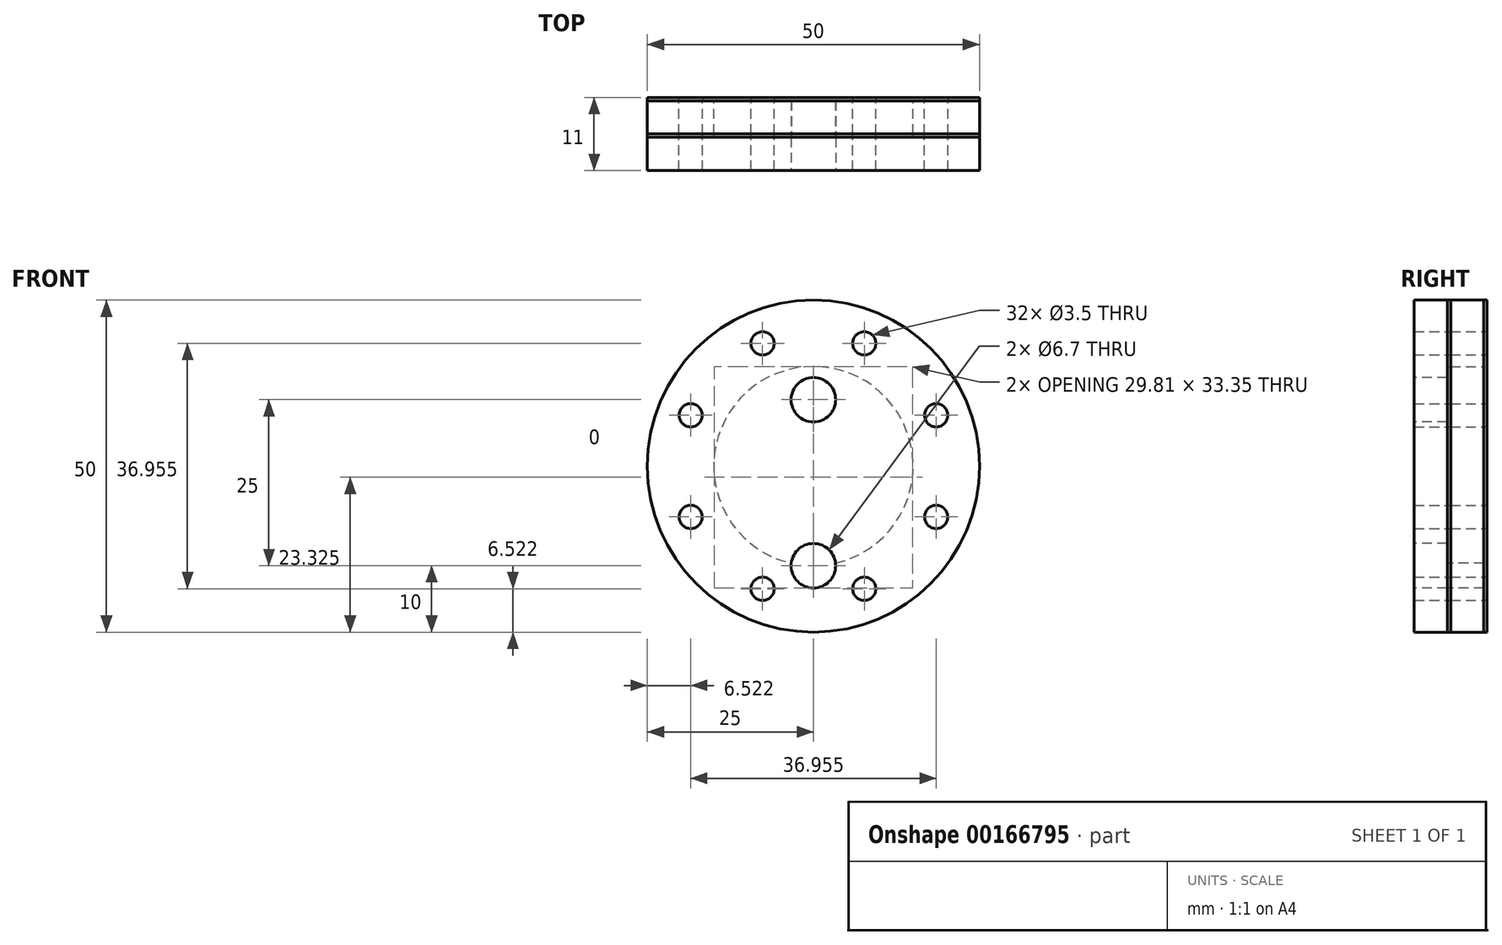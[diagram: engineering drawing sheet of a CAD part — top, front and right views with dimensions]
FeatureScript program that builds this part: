
annotation { "Feature Type Name" : "Feature", "Feature Type Description" : "" }
export const myFeature = defineFeature(function(context is Context, id is Id, definition is map)
    precondition{}
    {
        {
            var Q0;
            Q0=qCreatedBy(makeId("Front.planeOp"),FACE);
            var sketch = newSketch(context, id + "F0", { "sketchPlane" : qUnion([Q0])});
            skCircle(sketch, "E0", {"center": v(0, 0) * mm, "radius": 20 * mm, "construction": true});
            skCircle(sketch, "E1", {"center": v(7.65, -18.48) * mm, "radius": 1.75 * mm});
            skLineSegment(sketch, "E2", {"start": v(7.65, -18.48) * mm, "end": v(0, 0) * mm, "construction": true});
            skCircle(sketch, "E3.1.0", {"center": v(18.48, -7.65) * mm, "radius": 1.75 * mm});
            skCircle(sketch, "E3.2.0", {"center": v(18.48, 7.65) * mm, "radius": 1.75 * mm});
            skCircle(sketch, "E3.3.0", {"center": v(7.65, 18.48) * mm, "radius": 1.75 * mm});
            skCircle(sketch, "E3.4.0", {"center": v(-7.65, 18.48) * mm, "radius": 1.75 * mm});
            skCircle(sketch, "E3.5.0", {"center": v(-18.48, 7.65) * mm, "radius": 1.75 * mm});
            skCircle(sketch, "E3.6.0", {"center": v(-18.48, -7.65) * mm, "radius": 1.75 * mm});
            skCircle(sketch, "E3.7.0", {"center": v(-7.65, -18.48) * mm, "radius": 1.75 * mm});
            skSolve(sketch);
        }
        {
            var Q0;
            Q0=qCreatedBy(makeId("Front.planeOp"),FACE);
            var sketch = newSketch(context, id + "F1", { "sketchPlane" : qUnion([Q0])});
            skCircle(sketch, "E4", {"center": v(0, 0) * mm, "radius": 15 * mm});
            skCircle(sketch, "E5", {"center": v(0, 0) * mm, "radius": 25 * mm});
            skSolve(sketch);
        }
        {
            var Q0;
            Q0=makeQuery(id+"F1.imprint","IMPRINT",FACE,{"disambiguationData":[TD([[makeQuery(id+"F1.imprint","IMPRINT",EDGE,{"derivedFrom":sQuery(id+"F1.wireOp",EDGE,"E4")}),-1.0]])]});
            extrude(context, id + "F2", {"entities" : qUnion([Q0]), "depth" : 5 * mm});
        }
        {
            var Q0;
            Q0 = qSketchRegion(id + "F0", true);
            extrude(context, id + "F3", {"entities" : qUnion([Q0]), "operationType" : NewBodyOperationType.REMOVE, "endBound" : BoundingType.THROUGH_ALL, "depth" : 25 * mm});
        }
        {
            var Q0;
            Q0=makeQuery(id+"F2.opExtrude","CAP_FACE",FACE,{"disambiguationData":[OSD([sQuery(id+"F1.wireOp",EDGE,"E4"),sQuery(id+"F1.wireOp",EDGE,"E5")])],"isStart":false});
            extrude(context, id + "F4", {"entities" : qUnion([Q0]), "depth" : 0.5 * mm});
        }
        {
            var Q0;
            Q0=makeQuery(id+"F4.opExtrude","CAP_FACE",FACE,{"disambiguationData":[OSD([sQuery(id+"F1.wireOp",EDGE,"E4"),sQuery(id+"F1.wireOp",EDGE,"E5")])],"isStart":false});
            var sketch = newSketch(context, id + "F5", { "sketchPlane" : qUnion([Q0])});
            skCircle(sketch, "E6", {"center": v(0, 0) * mm, "radius": 25 * mm});
            skSolve(sketch);
        }
        {
            var Q0;
            Q0 = qSketchRegion(id + "F5", true);
            extrude(context, id + "F6", {"entities" : qUnion([Q0]), "depth" : 5 * mm});
        }
        {
            var Q0;
            Q0 = qSketchRegion(id + "F0", true);
            extrude(context, id + "F7", {"entities" : qUnion([Q0]), "operationType" : NewBodyOperationType.REMOVE, "endBound" : BoundingType.THROUGH_ALL, "depth" : 25 * mm});
        }
        {
            var Q0;
            Q0=makeQuery(id+"F6.opExtrude","CAP_FACE",FACE,{"disambiguationData":[OSD([sQuery(id+"F5.wireOp",EDGE,"E6")])],"isStart":false});
            var sketch = newSketch(context, id + "F8", { "sketchPlane" : qUnion([Q0])});
            skCircle(sketch, "E7", {"center": v(0, 10) * mm, "radius": 3.35 * mm});
            skCircle(sketch, "E8", {"center": v(0, -15) * mm, "radius": 3.35 * mm});
            skSolve(sketch);
        }
        {
            var Q0;
            Q0 = qSketchRegion(id + "F8", true);
            extrude(context, id + "F9", {"entities" : qUnion([Q0]), "operationType" : NewBodyOperationType.REMOVE, "endBound" : BoundingType.THROUGH_ALL, "oppositeDirection" : true, "depth" : 25 * mm});
        }
        {
            var Q0;
            Q0=makeQuery(id+"F4.opExtrude","CAP_FACE",FACE,{"disambiguationData":[OSD([sQuery(id+"F1.wireOp",EDGE,"E4"),sQuery(id+"F1.wireOp",EDGE,"E5")])],"isStart":false});
            var sketch = newSketch(context, id + "F10", { "sketchPlane" : qUnion([Q0])});
            skCircle(sketch, "E9", {"center": v(0, -15) * mm, "radius": 1.25 * mm});
            skSolve(sketch);
        }
        {
            var Q0;
            Q0 = qSketchRegion(id + "F10", true);
            extrude(context, id + "F11", {"entities" : qUnion([Q0]), "operationType" : NewBodyOperationType.REMOVE, "endBound" : BoundingType.THROUGH_ALL, "oppositeDirection" : true, "depth" : 25 * mm});
        }
        {
            var Q0;
            Q0=makeQuery(id+"F2.opExtrude","CAP_FACE",FACE,{"disambiguationData":[OSD([sQuery(id+"F1.wireOp",EDGE,"E4"),sQuery(id+"F1.wireOp",EDGE,"E5")])],"isStart":true});
            var sketch = newSketch(context, id + "F12", { "sketchPlane" : qUnion([Q0])});
            skCircle(sketch, "E10.0.0", {"center": v(0, 0) * mm, "radius": 25 * mm});
            skCircle(sketch, "E11.0", {"center": v(-18.48, 7.65) * mm, "radius": 1.75 * mm});
            skCircle(sketch, "E12.0", {"center": v(-7.65, 18.48) * mm, "radius": 1.75 * mm});
            skCircle(sketch, "E13.0", {"center": v(7.65, 18.48) * mm, "radius": 1.75 * mm});
            skCircle(sketch, "E14.0", {"center": v(18.48, 7.65) * mm, "radius": 1.75 * mm});
            skCircle(sketch, "E15.0", {"center": v(18.48, -7.65) * mm, "radius": 1.75 * mm});
            skCircle(sketch, "E16.0", {"center": v(7.65, -18.48) * mm, "radius": 1.75 * mm});
            skCircle(sketch, "E17.0", {"center": v(-7.65, -18.48) * mm, "radius": 1.75 * mm});
            skCircle(sketch, "E18.0", {"center": v(-18.48, -7.65) * mm, "radius": 1.75 * mm});
            skSolve(sketch);
        }
        {
            var Q0;
            Q0 = qSketchRegion(id + "F12", true);
            extrude(context, id + "F13", {"entities" : qUnion([Q0]), "depth" : 0.5 * mm});
        }
    });
